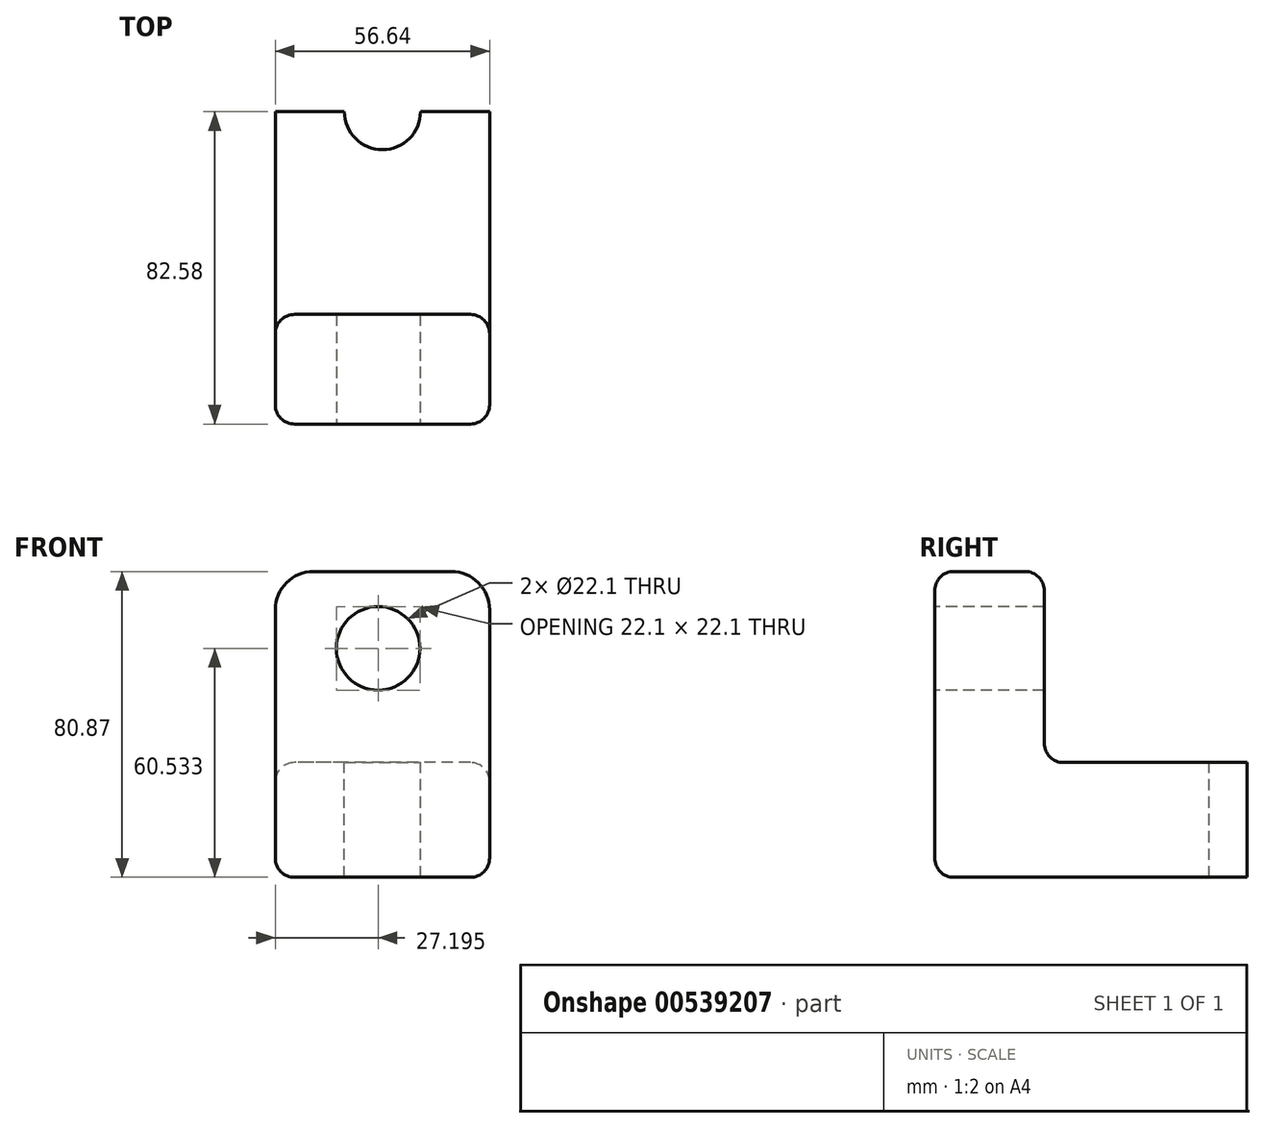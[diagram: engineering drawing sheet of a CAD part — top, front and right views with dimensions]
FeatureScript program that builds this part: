
annotation { "Feature Type Name" : "Feature", "Feature Type Description" : "" }
export const myFeature = defineFeature(function(context is Context, id is Id, definition is map)
    precondition{}
    {
        {
            var Q0;
            Q0=qCreatedBy(makeId("Right.planeOp"),FACE);
            var sketch = newSketch(context, id + "F0", { "sketchPlane" : qUnion([Q0])});
            skLineSegment(sketch, "E0", {"start": v(-15.47, 39.65) * mm, "end": v(13.5, 39.65) * mm});
            skLineSegment(sketch, "E1", {"start": v(13.5, 39.65) * mm, "end": v(13.5, -41.22) * mm});
            skLineSegment(sketch, "E2", {"start": v(13.5, -41.22) * mm, "end": v(-15.47, -41.22) * mm});
            skLineSegment(sketch, "E3", {"start": v(-15.47, -41.22) * mm, "end": v(-15.47, 39.65) * mm});
            skLineSegment(sketch, "E4", {"start": v(13.5, -10.87) * mm, "end": v(67.1, -10.87) * mm});
            skLineSegment(sketch, "E5", {"start": v(67.1, -10.87) * mm, "end": v(67.1, -41.22) * mm});
            skLineSegment(sketch, "E6", {"start": v(67.1, -41.22) * mm, "end": v(13.5, -41.22) * mm});
            skSolve(sketch);
        }
        {
            var Q0;
            Q0 = qSketchRegion(id + "F0", true);
            extrude(context, id + "F1", {"entities" : qUnion([Q0]), "depth" : 56.64 * mm, "offsetDistance" : 25.4 * mm});
        }
        {
            var Q0;
            Q0=makeQuery(id+"F1.opExtrude","SWEPT_FACE",FACE,{"disambiguationData":[OSD([sQuery(id+"F0.wireOp",EDGE,"E3")])]});
            var sketch = newSketch(context, id + "F2", { "sketchPlane" : qUnion([Q0])});
            skCircle(sketch, "E7", {"center": v(27.2, 19.31) * mm, "radius": 11.05 * mm});
            skSolve(sketch);
        }
        {
            var Q0;
            Q0 = qSketchRegion(id + "F0", true);
            extrude(context, id + "F3", {"entities" : qUnion([Q0]), "operationType" : NewBodyOperationType.REMOVE, "endBound" : BoundingType.THROUGH_ALL, "oppositeDirection" : true, "depth" : 25.4 * mm, "offsetDistance" : 25.4 * mm});
        }
        {
            var Q0;
            Q0=makeQuery(id+"F2.imprint","IMPRINT",FACE,{"disambiguationData":[TD([[makeQuery(id+"F2.imprint","IMPRINT",EDGE,{"derivedFrom":sQuery(id+"F2.wireOp",EDGE,"E7")}),1.0]])]});
            extrude(context, id + "F4", {"entities" : qUnion([Q0]), "operationType" : NewBodyOperationType.REMOVE, "endBound" : BoundingType.THROUGH_ALL, "oppositeDirection" : true, "depth" : 25.4 * mm, "offsetDistance" : 25.4 * mm});
        }
        {
            var Q0;
            Q0=makeQuery(id+"F1.opExtrude","SWEPT_FACE",FACE,{"disambiguationData":[OSD([sQuery(id+"F0.wireOp",EDGE,"E4")])]});
            var sketch = newSketch(context, id + "F5", { "sketchPlane" : qUnion([Q0])});
            skCircle(sketch, "E8", {"center": v(28.32, 67.1) * mm, "radius": 10.05 * mm});
            skSolve(sketch);
        }
        {
            var Q0;
            Q0 = qSketchRegion(id + "F5", true);
            extrude(context, id + "F6", {"entities" : qUnion([Q0]), "operationType" : NewBodyOperationType.REMOVE, "endBound" : BoundingType.THROUGH_ALL, "oppositeDirection" : true, "depth" : 25.4 * mm, "offsetDistance" : 25.4 * mm});
        }
        {
            var Q0;
            Q0=makeQuery(id+"F1.opExtrude","CAP_EDGE",EDGE,{"disambiguationData":[OSD([sQuery(id+"F0.wireOp",EDGE,"E1")])],"isStart":false});
            var Q1;
            Q1=makeQuery(id+"F1.opExtrude","CAP_EDGE",EDGE,{"disambiguationData":[OSD([sQuery(id+"F0.wireOp",EDGE,"E4")])],"isStart":false});
            var Q2;
            Q2=makeQuery(id+"F1.opExtrude","SWEPT_EDGE",EDGE,{"disambiguationData":[OSD([sQuery(id+"F0.wireOp",EDGE,"E0"),sQuery(id+"F0.wireOp",EDGE,"E1")])]});
            var Q3;
            Q3=makeQuery(id+"F1.opExtrude","SWEPT_EDGE",EDGE,{"disambiguationData":[OSD([sQuery(id+"F0.wireOp",EDGE,"E0"),sQuery(id+"F0.wireOp",EDGE,"E3")])]});
            var Q4;
            Q4=makeQuery(id+"F1.opExtrude","CAP_EDGE",EDGE,{"disambiguationData":[OSD([sQuery(id+"F0.wireOp",EDGE,"E4")])],"isStart":true});
            var Q5;
            Q5=makeQuery(id+"F1.opExtrude","CAP_EDGE",EDGE,{"disambiguationData":[OSD([sQuery(id+"F0.wireOp",EDGE,"E2"),sQuery(id+"F0.wireOp",EDGE,"E6")])],"isStart":false});
            var Q6;
            Q6=makeQuery(id+"F1.opExtrude","CAP_EDGE",EDGE,{"disambiguationData":[OSD([sQuery(id+"F0.wireOp",EDGE,"E1")])],"isStart":true});
            var Q7;
            Q7=makeQuery(id+"F1.opExtrude","CAP_EDGE",EDGE,{"disambiguationData":[OSD([sQuery(id+"F0.wireOp",EDGE,"E2"),sQuery(id+"F0.wireOp",EDGE,"E6")])],"isStart":true});
            var Q8;
            Q8=makeQuery(id+"F1.opExtrude","CAP_EDGE",EDGE,{"disambiguationData":[OSD([sQuery(id+"F0.wireOp",EDGE,"E3")])],"isStart":true});
            var Q9;
            Q9=makeQuery(id+"F1.opExtrude","SWEPT_EDGE",EDGE,{"disambiguationData":[OSD([sQuery(id+"F0.wireOp",EDGE,"E2"),sQuery(id+"F0.wireOp",EDGE,"E3")])]});
            var Q10;
            Q10=makeQuery(id+"F1.opExtrude","SWEPT_EDGE",EDGE,{"disambiguationData":[OSD([sQuery(id+"F0.wireOp",EDGE,"E1"),sQuery(id+"F0.wireOp",EDGE,"E4")])]});
            var Q11;
            Q11=makeQuery(id+"F1.opExtrude","CAP_EDGE",EDGE,{"disambiguationData":[OSD([sQuery(id+"F0.wireOp",EDGE,"E3")])],"isStart":false});
            fillet(context, id + "F7", {"entities" : qUnion([Q0, Q1, Q2, Q3, Q4, Q5, Q6, Q7, Q8, Q9, Q10, Q11]), "radius" : 5.08 * mm, "tangentPropagation" : true, "allowEdgeOverflow" : false});
        }
        {
            var Q0;
            Q0=makeQuery(id+"F1.opExtrude","CAP_EDGE",EDGE,{"disambiguationData":[OSD([sQuery(id+"F0.wireOp",EDGE,"E0")])],"isStart":false});
            var Q1;
            Q1=makeQuery(id+"F1.opExtrude","CAP_EDGE",EDGE,{"disambiguationData":[OSD([sQuery(id+"F0.wireOp",EDGE,"E0")])],"isStart":true});
            fillet(context, id + "F8", {"entities" : qUnion([Q0, Q1]), "radius" : 10.16 * mm, "tangentPropagation" : true, "allowEdgeOverflow" : false});
        }
    });
